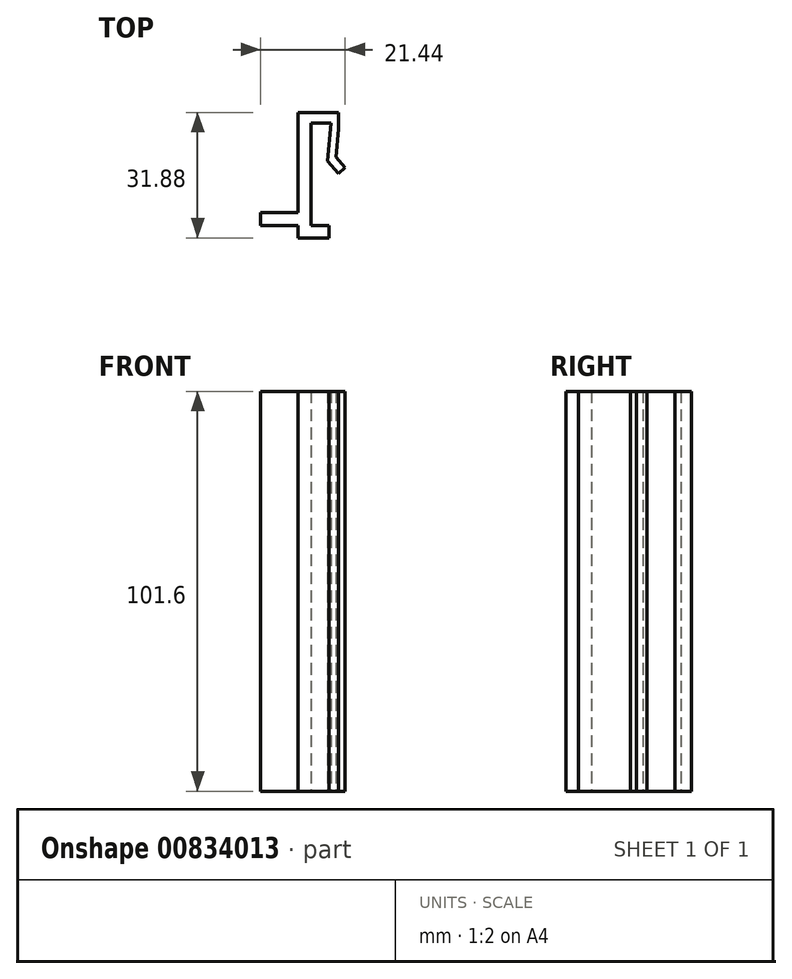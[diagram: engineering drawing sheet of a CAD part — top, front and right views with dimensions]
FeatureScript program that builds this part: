
annotation { "Feature Type Name" : "Feature", "Feature Type Description" : "" }
export const myFeature = defineFeature(function(context is Context, id is Id, definition is map)
    precondition{}
    {
        {
            var Q0;
            Q0=qCreatedBy(makeId("Top.planeOp"),FACE);
            var sketch = newSketch(context, id + "F0", { "sketchPlane" : qUnion([Q0])});
            skLineSegment(sketch, "E0", {"start": v(-19.4, 36.26) * mm, "end": v(-19.4, 10.23) * mm});
            skLineSegment(sketch, "E1", {"start": v(-19.4, 10.23) * mm, "end": v(-14.8, 10.23) * mm});
            skLineSegment(sketch, "E2", {"start": v(-14.8, 10.23) * mm, "end": v(-14.8, 7.05) * mm});
            skLineSegment(sketch, "E3", {"start": v(-14.8, 7.05) * mm, "end": v(-22.63, 7.05) * mm});
            skLineSegment(sketch, "E4", {"start": v(-22.63, 7.05) * mm, "end": v(-22.63, 10.23) * mm});
            skLineSegment(sketch, "E5", {"start": v(-22.63, 10.23) * mm, "end": v(-32.15, 10.23) * mm});
            skLineSegment(sketch, "E6", {"start": v(-32.15, 10.23) * mm, "end": v(-32.15, 13.53) * mm});
            skLineSegment(sketch, "E7", {"start": v(-32.15, 13.53) * mm, "end": v(-22.63, 13.53) * mm});
            skLineSegment(sketch, "E8", {"start": v(-22.63, 13.53) * mm, "end": v(-22.63, 38.93) * mm});
            skLineSegment(sketch, "E9", {"start": v(-22.63, 38.93) * mm, "end": v(-12.34, 38.93) * mm});
            skLineSegment(sketch, "E10", {"start": v(-19.4, 36.26) * mm, "end": v(-14.25, 36.26) * mm});
            skPoint(sketch, "E11", {"position": v(-19.4, 26.6) * mm});
            skPoint(sketch, "E12", {"position": v(-15.24, 26.6) * mm});
            skLineSegment(sketch, "E13", {"start": v(-14.25, 36.26) * mm, "end": v(-15.24, 26.6) * mm});
            skPoint(sketch, "E14", {"position": v(-12.42, 23.43) * mm});
            skLineSegment(sketch, "E15", {"start": v(-15.24, 26.6) * mm, "end": v(-12.42, 23.43) * mm});
            skLineSegment(sketch, "E16", {"start": v(-12.42, 23.43) * mm, "end": v(-10.7, 24.95) * mm});
            skLineSegment(sketch, "E17", {"start": v(-12.34, 38.93) * mm, "end": v(-12.34, 34.74) * mm});
            skPoint(sketch, "E18", {"position": v(-13.07, 27.61) * mm});
            skLineSegment(sketch, "E19", {"start": v(-13.07, 27.61) * mm, "end": v(-10.7, 24.95) * mm});
            skLineSegment(sketch, "E20", {"start": v(-13.07, 27.61) * mm, "end": v(-12.34, 34.74) * mm});
            skSolve(sketch);
        }
        {
            var Q0;
            Q0=makeQuery(id+"F0.imprint","IMPRINT",FACE,{"disambiguationData":[TD([[makeQuery(id+"F0.imprint","IMPRINT",EDGE,{"derivedFrom":sQuery(id+"F0.wireOp",EDGE,"E0")}),-1.0]])]});
            extrude(context, id + "F1", {"entities" : qUnion([Q0]), "depth" : 101.6 * mm, "offsetDistance" : 25.4 * mm});
        }
    });
